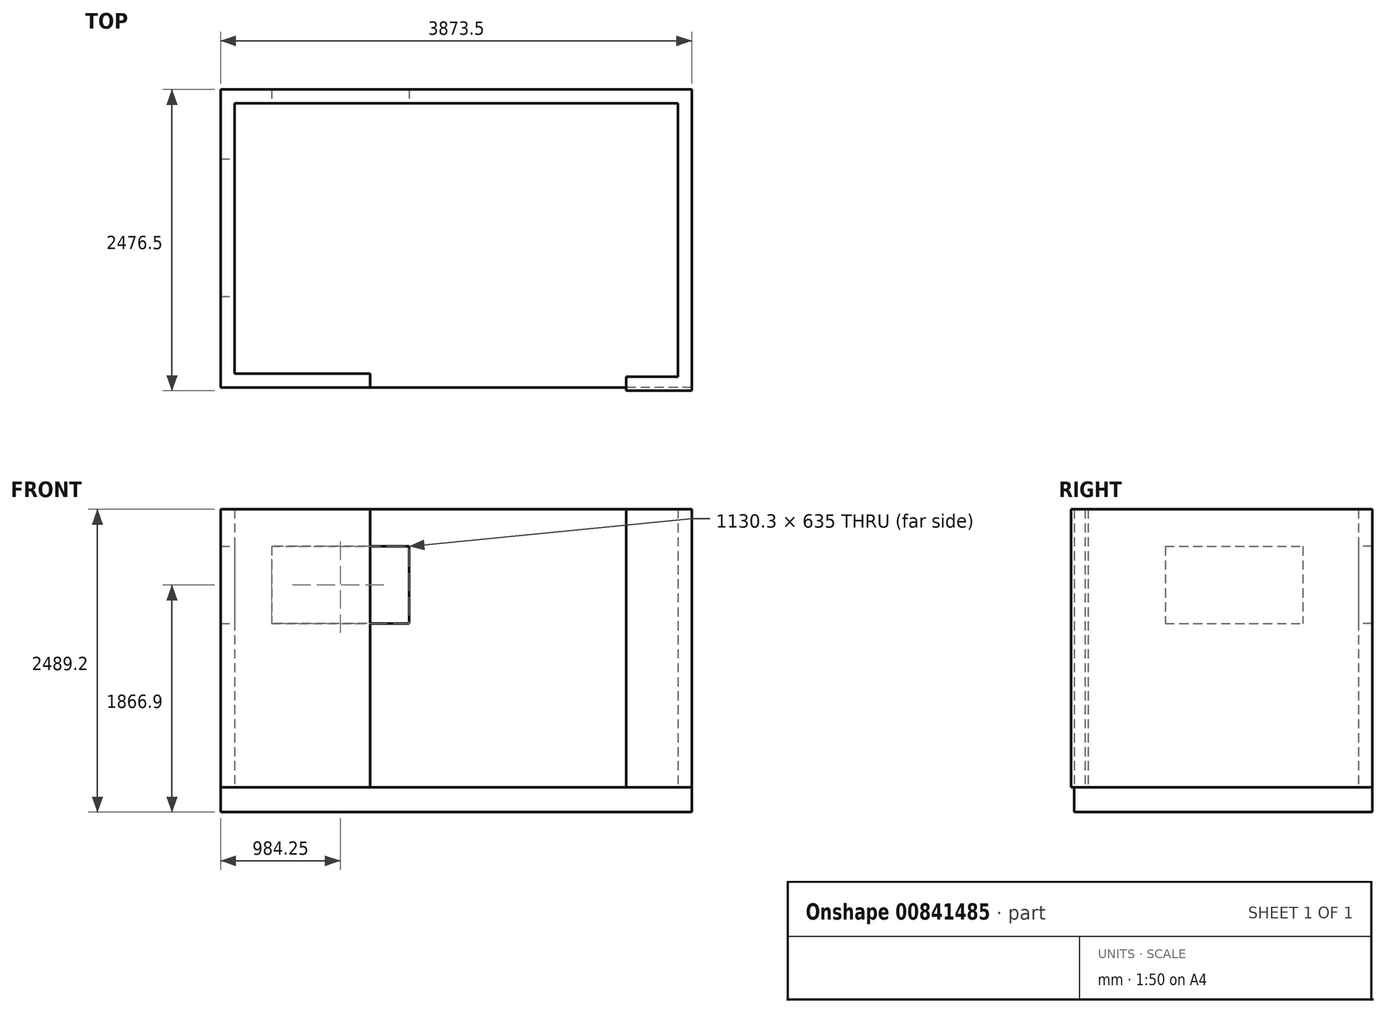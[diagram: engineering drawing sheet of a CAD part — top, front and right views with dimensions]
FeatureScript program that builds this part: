
annotation { "Feature Type Name" : "Feature", "Feature Type Description" : "" }
export const myFeature = defineFeature(function(context is Context, id is Id, definition is map)
    precondition{}
    {
        {
            var Q0;
            Q0=qCreatedBy(makeId("Top.planeOp"),FACE);
            var sketch = newSketch(context, id + "F0", { "sketchPlane" : qUnion([Q0])});
            skLineSegment(sketch, "E0.bottom", {"start": v(1936.75, -1225.55) * mm, "end": v(-1936.75, -1225.55) * mm});
            skLineSegment(sketch, "E0.top", {"start": v(1936.75, 1225.55) * mm, "end": v(-1936.75, 1225.55) * mm});
            skLineSegment(sketch, "E0.left", {"start": v(1936.75, -1225.55) * mm, "end": v(1936.75, 1225.55) * mm});
            skLineSegment(sketch, "E0.right", {"start": v(-1936.75, -1225.55) * mm, "end": v(-1936.75, 1225.55) * mm});
            skPoint(sketch, "E0.middle", {"position": v(0, 0) * mm});
            skSolve(sketch);
        }
        {
            var Q0;
            Q0 = qSketchRegion(id + "F0", true);
            extrude(context, id + "F1", {"entities" : qUnion([Q0]), "oppositeDirection" : true, "depth" : 203.2 * mm, "offsetDistance" : 25.4 * mm});
        }
        {
            var Q0;
            Q0=qCreatedBy(makeId("Top.planeOp"),FACE);
            var sketch = newSketch(context, id + "F2", { "sketchPlane" : qUnion([Q0])});
            skLineSegment(sketch, "E1.bottom", {"start": v(-1936.75, -1225.55) * mm, "end": v(-708.02, -1225.55) * mm});
            skLineSegment(sketch, "E1.top", {"start": v(-1936.75, -1111.25) * mm, "end": v(-708.02, -1111.25) * mm});
            skLineSegment(sketch, "E1.left", {"start": v(-1936.75, -1225.55) * mm, "end": v(-1936.75, -1111.25) * mm});
            skLineSegment(sketch, "E1.right", {"start": v(-708.02, -1225.55) * mm, "end": v(-708.02, -1111.25) * mm});
            skLineSegment(sketch, "E2.bottom", {"start": v(-1936.75, -1225.55) * mm, "end": v(-1822.45, -1225.55) * mm});
            skLineSegment(sketch, "E2.top", {"start": v(-1936.75, 1225.55) * mm, "end": v(-1822.45, 1225.55) * mm});
            skLineSegment(sketch, "E2.left", {"start": v(-1936.75, -1225.55) * mm, "end": v(-1936.75, 1225.55) * mm});
            skLineSegment(sketch, "E2.right", {"start": v(-1822.45, -1225.55) * mm, "end": v(-1822.45, 1225.55) * mm});
            skLineSegment(sketch, "E3.bottom", {"start": v(-1936.75, 1225.55) * mm, "end": v(1936.75, 1225.55) * mm});
            skLineSegment(sketch, "E3.top", {"start": v(-1936.75, 1111.25) * mm, "end": v(1936.75, 1111.25) * mm});
            skLineSegment(sketch, "E3.left", {"start": v(-1936.75, 1225.55) * mm, "end": v(-1936.75, 1111.25) * mm});
            skLineSegment(sketch, "E3.right", {"start": v(1936.75, 1225.55) * mm, "end": v(1936.75, 1111.25) * mm});
            skLineSegment(sketch, "E4.bottom", {"start": v(1936.75, 1225.55) * mm, "end": v(1822.45, 1225.55) * mm});
            skLineSegment(sketch, "E4.top", {"start": v(1936.75, -1250.95) * mm, "end": v(1822.45, -1250.95) * mm});
            skLineSegment(sketch, "E4.left", {"start": v(1936.75, 1225.55) * mm, "end": v(1936.75, -1250.95) * mm});
            skLineSegment(sketch, "E4.right", {"start": v(1822.45, 1225.55) * mm, "end": v(1822.45, -1250.95) * mm});
            skLineSegment(sketch, "E5.bottom", {"start": v(1936.75, -1250.95) * mm, "end": v(1397, -1250.95) * mm});
            skLineSegment(sketch, "E5.top", {"start": v(1936.75, -1136.65) * mm, "end": v(1397, -1136.65) * mm});
            skLineSegment(sketch, "E5.left", {"start": v(1936.75, -1250.95) * mm, "end": v(1936.75, -1136.65) * mm});
            skLineSegment(sketch, "E5.right", {"start": v(1397, -1250.95) * mm, "end": v(1397, -1136.65) * mm});
            skSolve(sketch);
        }
        {
            var Q0;
            Q0 = qSketchRegion(id + "F2", true);
            extrude(context, id + "F3", {"entities" : qUnion([Q0]), "depth" : 2286 * mm, "offsetDistance" : 25.4 * mm});
        }
        {
            var Q0;
            Q0=makeQuery(id+"F3.opExtrude","SWEPT_FACE",FACE,{"disambiguationData":[OSD([sQuery(id+"F2.wireOp",EDGE,"E3.top")])]});
            var sketch = newSketch(context, id + "F4", { "sketchPlane" : qUnion([Q0])});
            skLineSegment(sketch, "E6.bottom", {"start": v(-1517.65, 1981.2) * mm, "end": v(-387.35, 1981.2) * mm});
            skLineSegment(sketch, "E6.top", {"start": v(-1517.65, 1346.2) * mm, "end": v(-387.35, 1346.2) * mm});
            skLineSegment(sketch, "E6.left", {"start": v(-1517.65, 1981.2) * mm, "end": v(-1517.65, 1346.2) * mm});
            skLineSegment(sketch, "E6.right", {"start": v(-387.35, 1981.2) * mm, "end": v(-387.35, 1346.2) * mm});
            skSolve(sketch);
        }
        {
            var Q0;
            Q0 = qSketchRegion(id + "F4", true);
            extrude(context, id + "F5", {"entities" : qUnion([Q0]), "operationType" : NewBodyOperationType.REMOVE, "endBound" : BoundingType.THROUGH_ALL, "oppositeDirection" : true, "depth" : 25.4 * mm, "offsetDistance" : 25.4 * mm});
        }
        {
            var Q0;
            Q0=makeQuery(id+"F3.opExtrude","SWEPT_FACE",FACE,{"disambiguationData":[OSD([sQuery(id+"F2.wireOp",EDGE,"E2.right")])]});
            var sketch = newSketch(context, id + "F6", { "sketchPlane" : qUnion([Q0])});
            skLineSegment(sketch, "E7.bottom", {"start": v(-476.25, 1981.2) * mm, "end": v(654.05, 1981.2) * mm});
            skLineSegment(sketch, "E7.top", {"start": v(-476.25, 1346.2) * mm, "end": v(654.05, 1346.2) * mm});
            skLineSegment(sketch, "E7.left", {"start": v(-476.25, 1981.2) * mm, "end": v(-476.25, 1346.2) * mm});
            skLineSegment(sketch, "E7.right", {"start": v(654.05, 1981.2) * mm, "end": v(654.05, 1346.2) * mm});
            skSolve(sketch);
        }
        {
            var Q0;
            Q0 = qSketchRegion(id + "F6", true);
            extrude(context, id + "F7", {"entities" : qUnion([Q0]), "operationType" : NewBodyOperationType.REMOVE, "endBound" : BoundingType.THROUGH_ALL, "oppositeDirection" : true, "depth" : 25.4 * mm, "offsetDistance" : 25.4 * mm});
        }
    });
